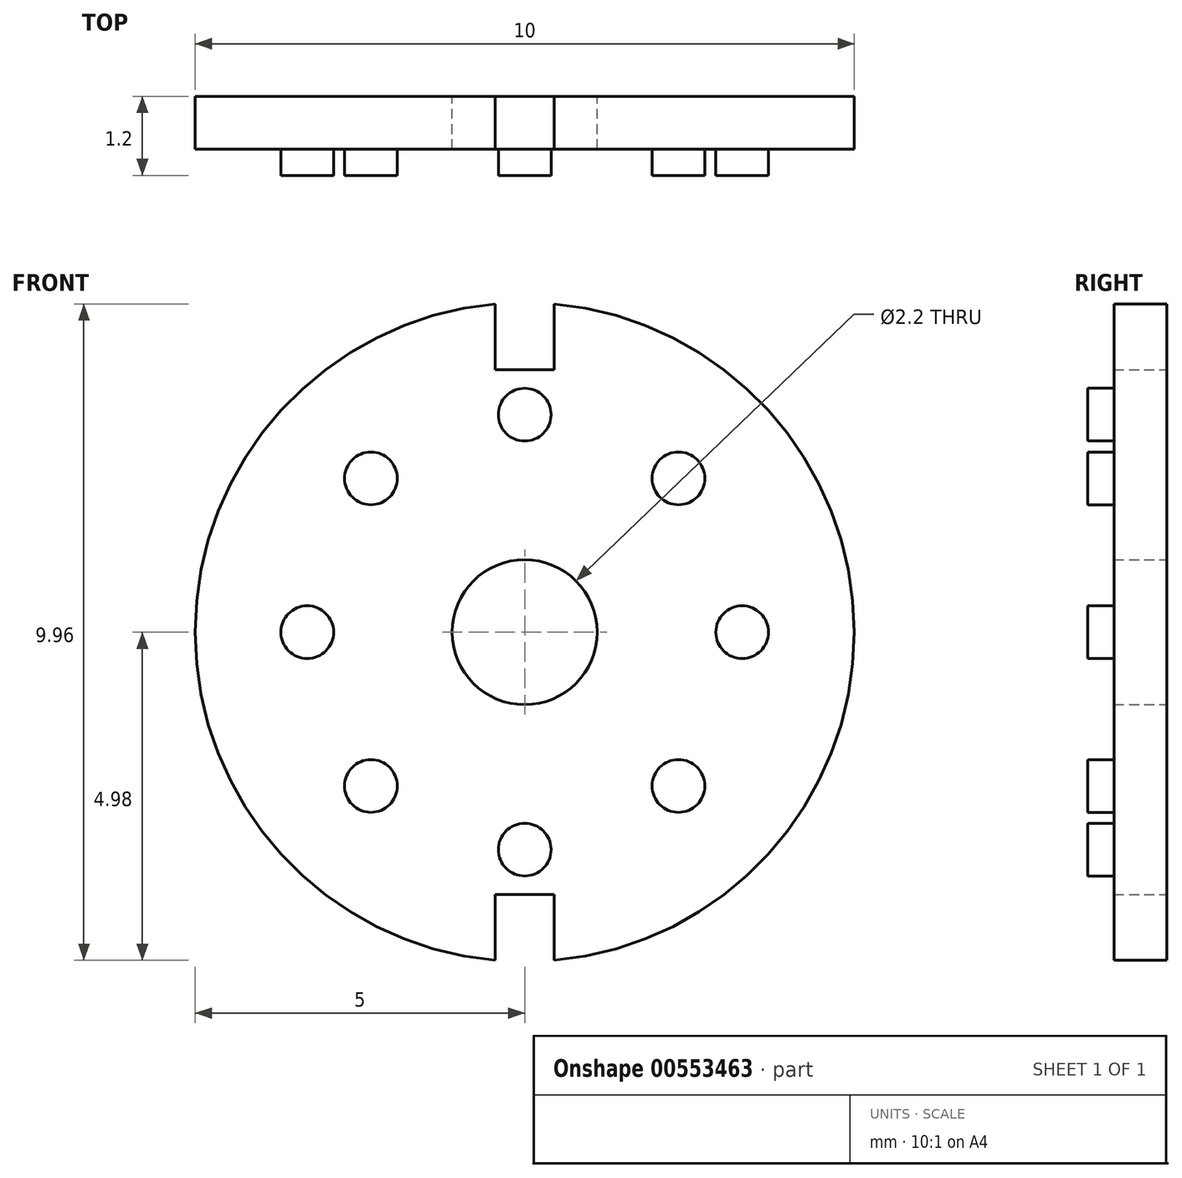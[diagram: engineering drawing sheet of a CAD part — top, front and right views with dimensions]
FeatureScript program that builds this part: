
annotation { "Feature Type Name" : "Feature", "Feature Type Description" : "" }
export const myFeature = defineFeature(function(context is Context, id is Id, definition is map)
    precondition{}
    {
        {
            var Q0;
            Q0=qCreatedBy(makeId("Front.planeOp"),FACE);
            var sketch = newSketch(context, id + "F0", { "sketchPlane" : qUnion([Q0])});
            skArc(sketch, "E0", {"start": v(-0.45, 4.98) * mm, "mid": v(-5, 0) * mm, "end": v(-0.45, -4.98) * mm});
            skCircle(sketch, "E1", {"center": v(0, 0) * mm, "radius": 1.1 * mm});
            skLineSegment(sketch, "E2.top", {"start": v(-0.45, 3.98) * mm, "end": v(0.45, 3.98) * mm});
            skLineSegment(sketch, "E2.left", {"start": v(-0.45, 4.98) * mm, "end": v(-0.45, 3.98) * mm});
            skLineSegment(sketch, "E2.right", {"start": v(0.45, 4.98) * mm, "end": v(0.45, 3.98) * mm});
            skLineSegment(sketch, "E3.top", {"start": v(-0.45, -3.98) * mm, "end": v(0.45, -3.98) * mm});
            skLineSegment(sketch, "E3.left", {"start": v(-0.45, -4.98) * mm, "end": v(-0.45, -3.98) * mm});
            skLineSegment(sketch, "E3.right", {"start": v(0.45, -4.98) * mm, "end": v(0.45, -3.98) * mm});
            skArc(sketch, "E4.trimOffspring", {"start": v(0.45, -4.98) * mm, "mid": v(5, 0) * mm, "end": v(0.45, 4.98) * mm});
            skSolve(sketch);
        }
        {
            var Q0;
            Q0 = qSketchRegion(id + "F0", true);
            extrude(context, id + "F1", {"entities" : qUnion([Q0]), "depth" : 0.8 * mm, "offsetDistance" : 25 * mm});
        }
        {
            var Q0;
            Q0=makeQuery(id+"F1.opExtrude","CAP_FACE",FACE,{"disambiguationData":[OSD([sQuery(id+"F0.wireOp",EDGE,"E0")])],"isStart":false});
            var sketch = newSketch(context, id + "F2", { "sketchPlane" : qUnion([Q0])});
            skCircle(sketch, "E5", {"center": v(0, 3.3) * mm, "radius": 0.4 * mm});
            skSolve(sketch);
        }
        {
            var Q0;
            Q0 = qSketchRegion(id + "F2", true);
            extrude(context, id + "F3", {"entities" : qUnion([Q0]), "depth" : 0.4 * mm, "offsetDistance" : 25 * mm});
        }
        {
            var Q0;
            Q0=makeQuery(id+"F3.opExtrude","SWEPT_BODY",BODY,{"disambiguationData":[OSD([sQuery(id+"F2.wireOp",EDGE,"E5")])]});
            var Q1;
            Q1=makeQuery(id+"F1.opExtrude","CAP_EDGE",EDGE,{"disambiguationData":[OSD([sQuery(id+"F0.wireOp",EDGE,"E0")])],"isStart":false});
            circularPattern(context, id + "F4", {"entities" : qUnion([Q0]), "axis" : qUnion([Q1]), "angle" : 360 * degree, "instanceCount" : 8, "equalSpace" : true});
        }
    });
